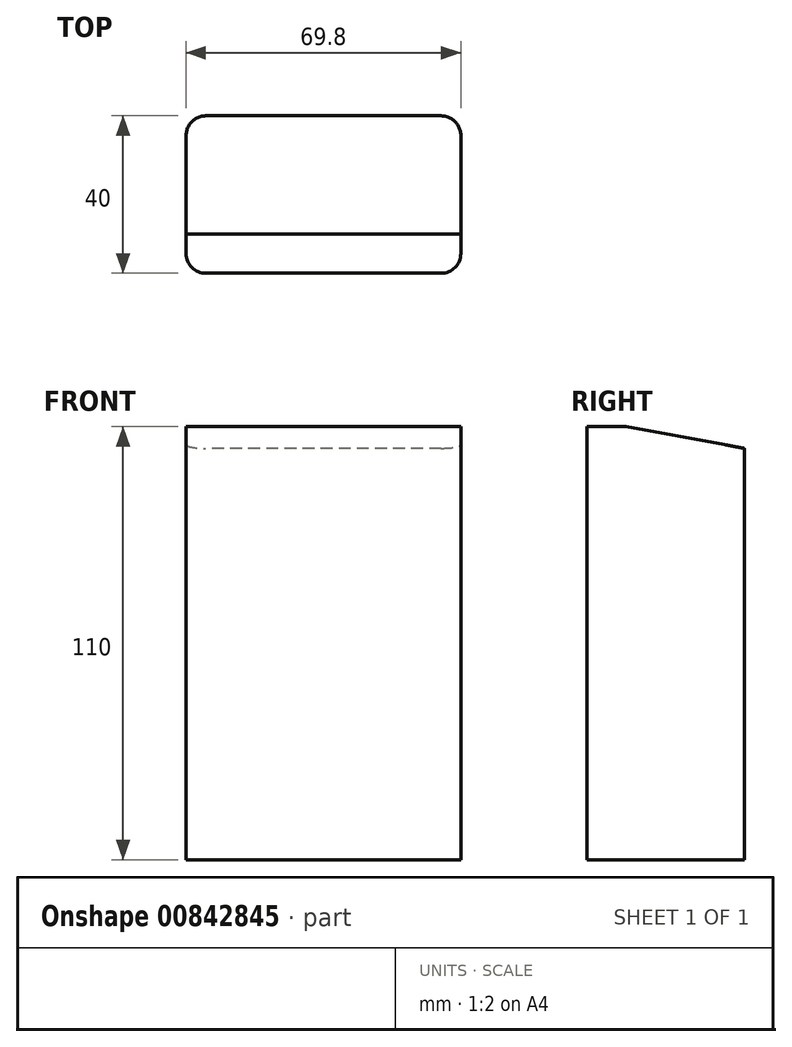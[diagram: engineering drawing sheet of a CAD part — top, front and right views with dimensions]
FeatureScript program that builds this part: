
annotation { "Feature Type Name" : "Feature", "Feature Type Description" : "" }
export const myFeature = defineFeature(function(context is Context, id is Id, definition is map)
    precondition{}
    {
        {
            var Q0;
            Q0=qCreatedBy(makeId("Top.planeOp"),FACE);
            var sketch = newSketch(context, id + "F0", { "sketchPlane" : qUnion([Q0])});
            skLineSegment(sketch, "E0.bottom", {"start": v(-29.9, -20) * mm, "end": v(29.9, -20) * mm});
            skLineSegment(sketch, "E0.top", {"start": v(-29.9, 20) * mm, "end": v(29.9, 20) * mm});
            skLineSegment(sketch, "E0.left", {"start": v(-34.9, -15) * mm, "end": v(-34.9, 15) * mm});
            skLineSegment(sketch, "E0.right", {"start": v(34.9, -15) * mm, "end": v(34.9, 15) * mm});
            skPoint(sketch, "E0.middle", {"position": v(0, 0) * mm});
            skPoint(sketch, "E1.visualSharp", {"position": v(-34.9, -20) * mm});
            skArc(sketch, "E1.filletArc", {"start": v(-34.9, -15) * mm, "mid": v(-33.43, -18.54) * mm, "end": v(-29.9, -20) * mm});
            skPoint(sketch, "E2.visualSharp", {"position": v(34.9, -20) * mm});
            skArc(sketch, "E2.filletArc", {"start": v(29.9, -20) * mm, "mid": v(33.43, -18.54) * mm, "end": v(34.9, -15) * mm});
            skPoint(sketch, "E3.visualSharp", {"position": v(34.9, 20) * mm});
            skArc(sketch, "E3.filletArc", {"start": v(34.9, 15) * mm, "mid": v(33.43, 18.54) * mm, "end": v(29.9, 20) * mm});
            skPoint(sketch, "E4.visualSharp", {"position": v(-34.9, 20) * mm});
            skArc(sketch, "E4.filletArc", {"start": v(-29.9, 20) * mm, "mid": v(-33.43, 18.54) * mm, "end": v(-34.9, 15) * mm});
            skSolve(sketch);
        }
        {
            var Q0;
            Q0=makeQuery(id+"F0.imprint","IMPRINT",FACE,{"disambiguationData":[TD([[makeQuery(id+"F0.imprint","IMPRINT",EDGE,{"derivedFrom":sQuery(id+"F0.wireOp",EDGE,"E0.bottom")}),1.0]])]});
            extrude(context, id + "F1", {"entities" : qUnion([Q0]), "depth" : 110 * mm, "offsetDistance" : 25 * mm});
        }
        {
            var Q0;
            Q0=makeQuery(id+"F1.opExtrude","SWEPT_FACE",FACE,{"disambiguationData":[OSD([sQuery(id+"F0.wireOp",EDGE,"E0.left")])]});
            var sketch = newSketch(context, id + "F2", { "sketchPlane" : qUnion([Q0])});
            skLineSegment(sketch, "E5", {"start": v(-20.88, 104.36) * mm, "end": v(-20.88, 110) * mm});
            skLineSegment(sketch, "E6", {"start": v(-20.88, 104.36) * mm, "end": v(10.08, 110) * mm});
            skLineSegment(sketch, "E7", {"start": v(10.08, 110) * mm, "end": v(-20.88, 110) * mm});
            skSolve(sketch);
        }
        {
            var Q0;
            Q0 = qSketchRegion(id + "F2", true);
            extrude(context, id + "F3", {"entities" : qUnion([Q0]), "operationType" : NewBodyOperationType.REMOVE, "endBound" : BoundingType.THROUGH_ALL, "oppositeDirection" : true, "depth" : 25 * mm, "offsetDistance" : 25 * mm});
        }
    });
